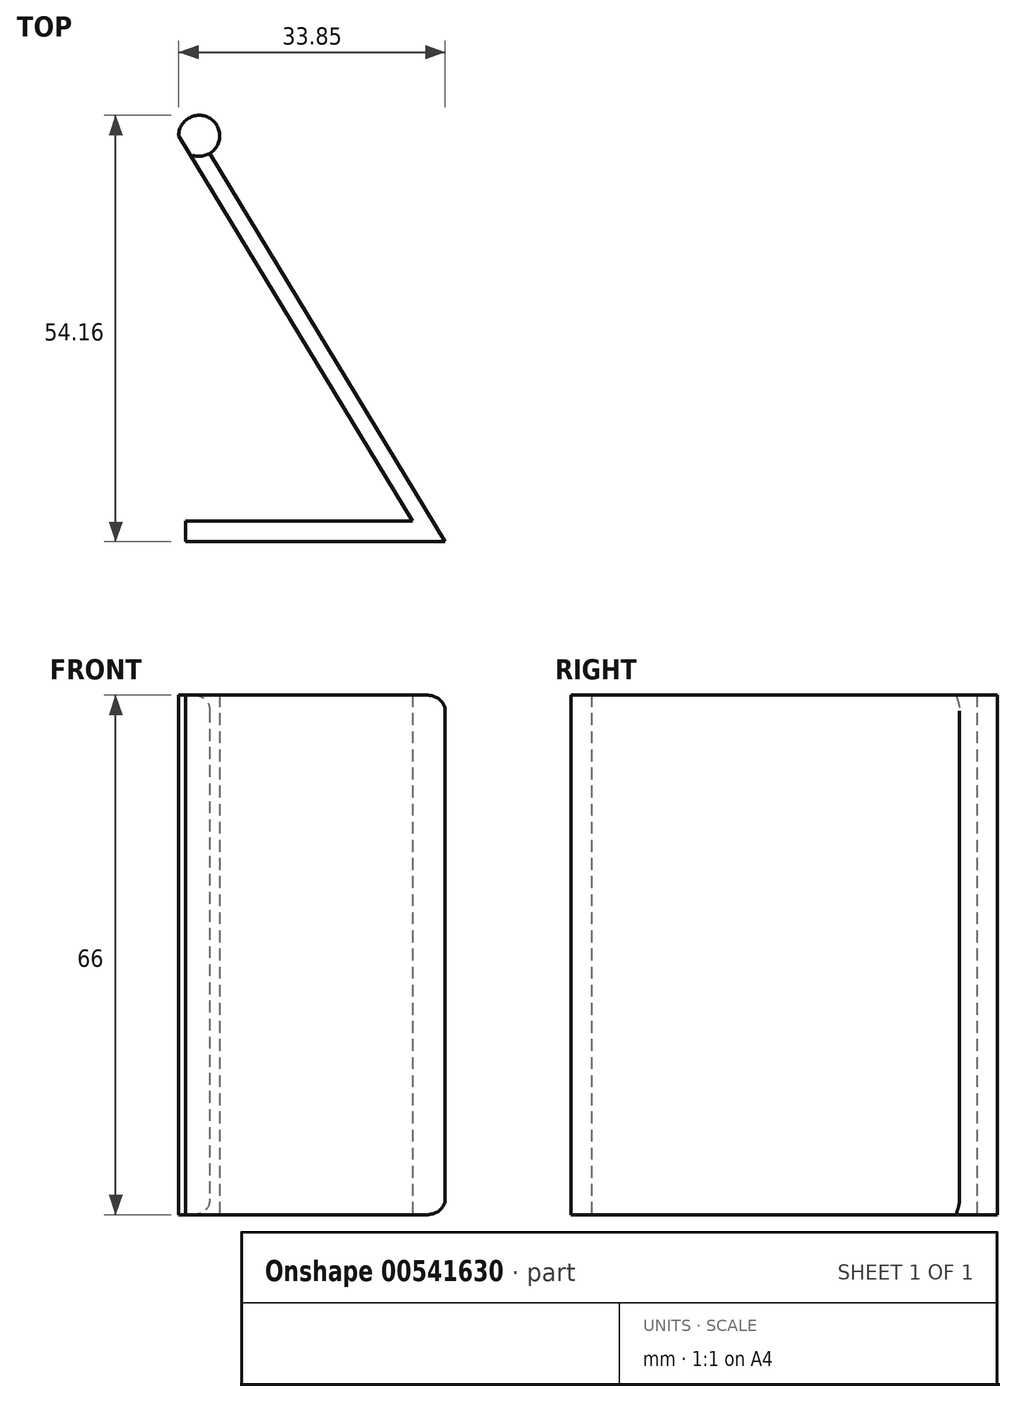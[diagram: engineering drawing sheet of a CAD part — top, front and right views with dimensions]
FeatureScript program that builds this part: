
annotation { "Feature Type Name" : "Feature", "Feature Type Description" : "" }
export const myFeature = defineFeature(function(context is Context, id is Id, definition is map)
    precondition{}
    {
        {
            var Q0;
            Q0=qCreatedBy(makeId("Top.planeOp"),FACE);
            var sketch = newSketch(context, id + "F0", { "sketchPlane" : qUnion([Q0])});
            skLineSegment(sketch, "E0", {"start": v(0, 0) * mm, "end": v(-33, 0) * mm});
            skLineSegment(sketch, "E1", {"start": v(-33, 0) * mm, "end": v(-33, 2.6) * mm});
            skLineSegment(sketch, "E2", {"start": v(-33, 2.6) * mm, "end": v(-1.58, 2.6) * mm});
            skLineSegment(sketch, "E3", {"start": v(0, 0) * mm, "end": v(-31.25, 51.56) * mm});
            skLineSegment(sketch, "E4", {"start": v(-31.25, 51.56) * mm, "end": v(-33.85, 51.56) * mm});
            skLineSegment(sketch, "E5", {"start": v(-33.85, 51.56) * mm, "end": v(-4.18, 2.6) * mm});
            skCircle(sketch, "E6", {"center": v(-31.25, 51.56) * mm, "radius": 2.6 * mm});
            skPoint(sketch, "E7.start.orphan", {"position": v(0, 2.6) * mm});
            skSolve(sketch);
        }
        {
            var Q0;
            {var subQ0=sQuery(id+"F0.wireOp",EDGE,"E5");var subQ1=sQuery(id+"F0.wireOp",EDGE,"E2");var subQ2=makeQuery(id+"F0.imprint","INTERSECT",VERTEX,{"derivedFrom":[subQ1,subQ0]});Q0=makeQuery(id+"F0.imprint","IMPRINT",FACE,{"disambiguationData":[TD([[makeQuery(id+"F0.imprint","IMPRINT",EDGE,{"disambiguationData":[TD([[subQ2,-1.0]])],"derivedFrom":subQ1}),1.0]])]});}
            var Q1;
            {var subQ0=sQuery(id+"F0.wireOp",EDGE,"E4");Q1=makeQuery(id+"F0.imprint","IMPRINT",FACE,{"disambiguationData":[TD([[makeQuery(id+"F0.imprint","IMPRINT",EDGE,{"derivedFrom":subQ0}),-1.0]])]});}
            var Q2;
            {var subQ0=sQuery(id+"F0.wireOp",EDGE,"E4");Q2=makeQuery(id+"F0.imprint","IMPRINT",FACE,{"disambiguationData":[TD([[makeQuery(id+"F0.imprint","IMPRINT",EDGE,{"derivedFrom":subQ0}),1.0]])]});}
            var Q3;
            {var subQ5=sQuery(id+"F0.wireOp",EDGE,"E0");Q3=makeQuery(id+"F0.imprint","IMPRINT",FACE,{"disambiguationData":[TD([[makeQuery(id+"F0.imprint","IMPRINT",EDGE,{"derivedFrom":subQ5}),-1.0]])]});}
            extrude(context, id + "F1", {"entities" : qUnion([Q0, Q1, Q2, Q3]), "depth" : 66 * mm, "offsetDistance" : 25 * mm});
        }
        {
            var Q0;
            Q0=makeQuery(id+"F1.opExtrude","CAP_EDGE",EDGE,{"disambiguationData":[OSD([sQuery(id+"F0.wireOp",EDGE,"E3")])],"isStart":false});
            var Q1;
            Q1=makeQuery(id+"F1.opExtrude","CAP_EDGE",EDGE,{"disambiguationData":[OSD([sQuery(id+"F0.wireOp",EDGE,"E3")])],"isStart":true});
            fillet(context, id + "F2", {"entities" : qUnion([Q0, Q1]), "radius" : 2 * mm, "tangentPropagation" : true, "allowEdgeOverflow" : false});
        }
    });
